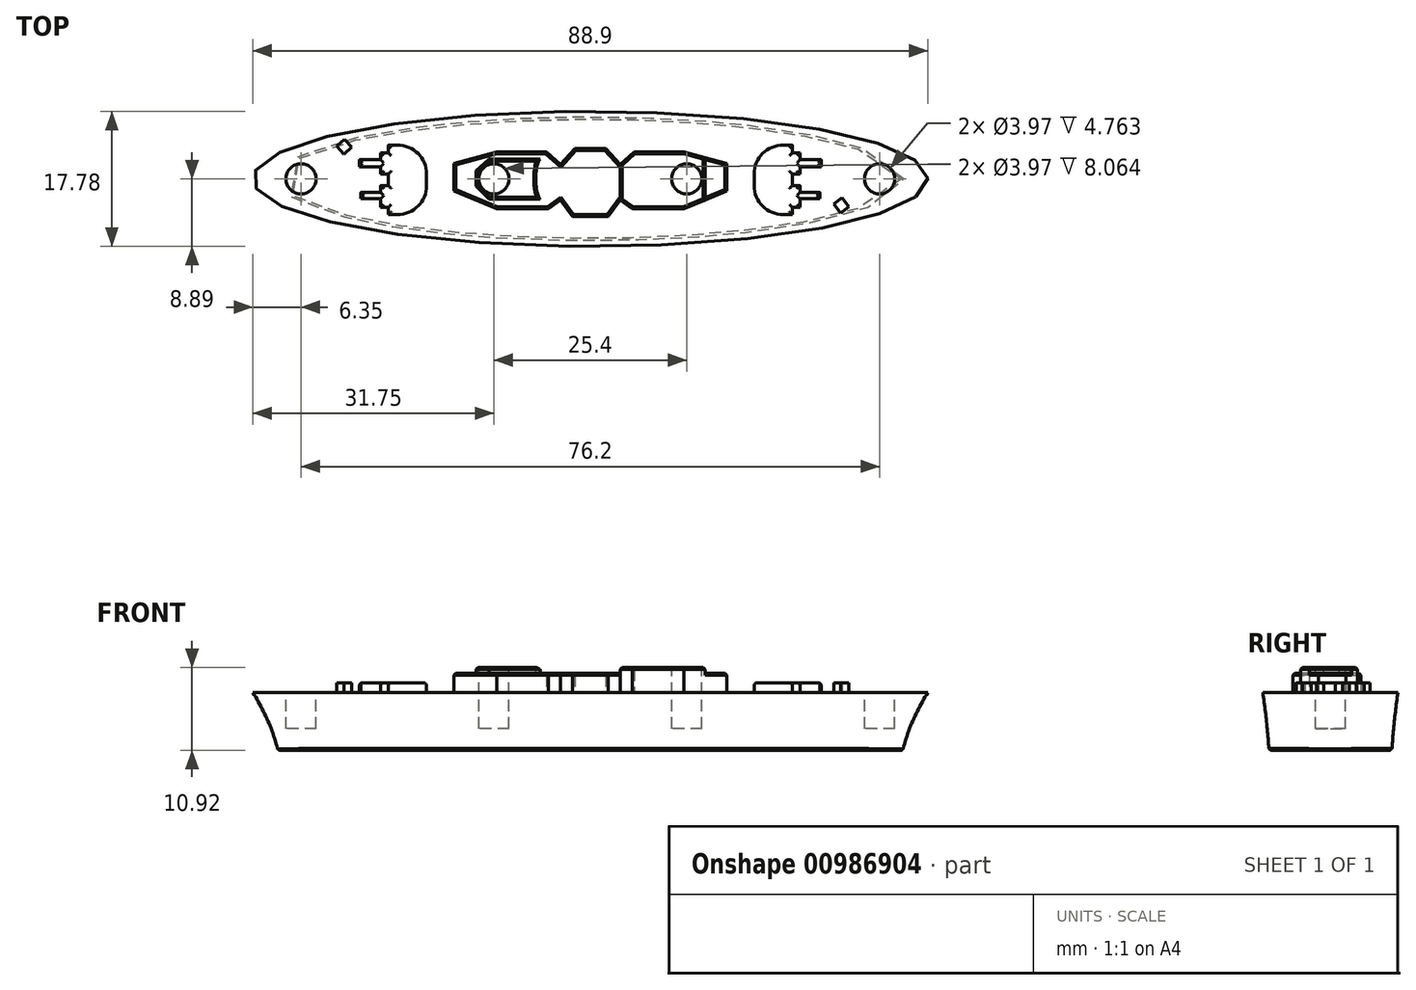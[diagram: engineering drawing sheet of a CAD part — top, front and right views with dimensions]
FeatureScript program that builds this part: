
annotation { "Feature Type Name" : "Feature", "Feature Type Description" : "" }
export const myFeature = defineFeature(function(context is Context, id is Id, definition is map)
    precondition{}
    {
        {
            var Q0;
            Q0=qCreatedBy(makeId("Top.planeOp"),FACE);
            var sketch = newSketch(context, id + "F0", { "sketchPlane" : qUnion([Q0])});
            skEllipse(sketch, "E0", {"center": v(0, 0) * mm, "majorRadius": 44.45 * mm, "minorRadius": 8.9 * mm, "majorAxis": v(1, 0)});
            skSolve(sketch);
        }
        {
            var Q0;
            Q0=qCreatedBy(makeId("Top.planeOp"),FACE);
            cPlane(context, id + "F1", {"entities" : qUnion([Q0]), "cplaneType" : CPlaneType.OFFSET, "offset" : 7.62 * mm, "oppositeDirection" : true, "width" : 152.4 * mm, "height" : 152.4 * mm});
        }
        {
            var Q0;
            Q0=qCreatedBy(id+"F1.planeOp",FACE);
            var sketch = newSketch(context, id + "F2", { "sketchPlane" : qUnion([Q0])});
            skEllipse(sketch, "E1", {"center": v(0, 0) * mm, "majorRadius": 41.16 * mm, "minorRadius": 8.1 * mm, "majorAxis": v(1, 0)});
            skSolve(sketch);
        }
        {
            var Q0;
            Q0=makeQuery(id+"F2.imprint","IMPRINT",FACE,{"disambiguationData":[TD([[makeQuery(id+"F2.imprint","IMPRINT",EDGE,{"derivedFrom":sQuery(id+"F2.wireOp",EDGE,"E1")}),1.0]])]});
            var Q1;
            Q1=makeQuery(id+"F0.imprint","IMPRINT",FACE,{"disambiguationData":[TD([[makeQuery(id+"F0.imprint","IMPRINT",EDGE,{"derivedFrom":sQuery(id+"F0.wireOp",EDGE,"E0")}),1.0]])]});
            loft(context, id + "F3", {"sheetProfilesArray" : [{ "sheetProfileEntities" : qUnion([Q0]) }, { "sheetProfileEntities" : qUnion([Q1]) }]});
        }
        {
            var Q0;
            Q0=makeQuery(id+"F3.opLoft","CAP_FACE",FACE,{"disambiguationData":[OSD([makeQuery(id+"F0.imprint","IMPRINT",FACE,{"disambiguationData":[TD([[makeQuery(id+"F0.imprint","IMPRINT",EDGE,{"derivedFrom":sQuery(id+"F0.wireOp",EDGE,"E0")}),1.0]])]})])],"isStart":true});
            var sketch = newSketch(context, id + "F4", { "sketchPlane" : qUnion([Q0])});
            skLineSegment(sketch, "E2", {"start": v(-38.1, 0) * mm, "end": v(-12.7, 0) * mm, "construction": true});
            skLineSegment(sketch, "E3", {"start": v(-12.7, 0) * mm, "end": v(12.7, 0) * mm, "construction": true});
            skLineSegment(sketch, "E4", {"start": v(12.7, 0) * mm, "end": v(38.1, 0) * mm, "construction": true});
            skCircle(sketch, "E5", {"center": v(38.1, 0) * mm, "radius": 1.98 * mm});
            skCircle(sketch, "E6", {"center": v(12.7, 0) * mm, "radius": 1.98 * mm});
            skCircle(sketch, "E7", {"center": v(-12.7, 0) * mm, "radius": 1.98 * mm});
            skCircle(sketch, "E8", {"center": v(-38.1, 0) * mm, "radius": 1.98 * mm});
            skSolve(sketch);
        }
        {
            var Q0;
            Q0=makeQuery(id+"F4.imprint","IMPRINT",FACE,{"disambiguationData":[TD([[makeQuery(id+"F4.imprint","IMPRINT",EDGE,{"derivedFrom":sQuery(id+"F4.wireOp",EDGE,"E8")}),1.0]])]});
            var Q1;
            Q1=makeQuery(id+"F4.imprint","IMPRINT",FACE,{"disambiguationData":[TD([[makeQuery(id+"F4.imprint","IMPRINT",EDGE,{"derivedFrom":sQuery(id+"F4.wireOp",EDGE,"E7")}),1.0]])]});
            var Q2;
            Q2=makeQuery(id+"F4.imprint","IMPRINT",FACE,{"disambiguationData":[TD([[makeQuery(id+"F4.imprint","IMPRINT",EDGE,{"derivedFrom":sQuery(id+"F4.wireOp",EDGE,"E6")}),1.0]])]});
            var Q3;
            Q3=makeQuery(id+"F4.imprint","IMPRINT",FACE,{"disambiguationData":[TD([[makeQuery(id+"F4.imprint","IMPRINT",EDGE,{"derivedFrom":sQuery(id+"F4.wireOp",EDGE,"E5")}),1.0]])]});
            extrude(context, id + "F5", {"entities" : qUnion([Q0, Q1, Q2, Q3]), "operationType" : NewBodyOperationType.REMOVE, "oppositeDirection" : true, "depth" : 4.76 * mm, "offsetDistance" : 25.4 * mm});
        }
        {
            var Q0;
            Q0=makeQuery(id+"F3.opLoft","CAP_FACE",FACE,{"disambiguationData":[OSD([makeQuery(id+"F0.imprint","IMPRINT",FACE,{"disambiguationData":[TD([[makeQuery(id+"F0.imprint","IMPRINT",EDGE,{"derivedFrom":sQuery(id+"F0.wireOp",EDGE,"E0")}),1.0]])]})])],"isStart":true});
            var sketch = newSketch(context, id + "F6", { "sketchPlane" : qUnion([Q0])});
            skLineSegment(sketch, "E9", {"start": v(0, 11.72) * mm, "end": v(0, 15.23) * mm, "construction": true});
            skLineSegment(sketch, "E10", {"start": v(0, 4) * mm, "end": v(2.05, 4) * mm});
            skLineSegment(sketch, "E11", {"start": v(2.05, 4) * mm, "end": v(3.92, 1.9) * mm});
            skLineSegment(sketch, "E12", {"start": v(3.92, 1.9) * mm, "end": v(5.78, 3.55) * mm});
            skLineSegment(sketch, "E13", {"start": v(5.78, 3.55) * mm, "end": v(12.33, 3.55) * mm});
            skLineSegment(sketch, "E14", {"start": v(12.33, 3.55) * mm, "end": v(17.96, 2.05) * mm});
            skLineSegment(sketch, "E15", {"start": v(17.96, 2.05) * mm, "end": v(17.96, -1.6) * mm});
            skLineSegment(sketch, "E16", {"start": v(17.96, -1.6) * mm, "end": v(12.33, -3.94) * mm});
            skLineSegment(sketch, "E17", {"start": v(12.33, -3.94) * mm, "end": v(5.55, -3.94) * mm});
            skLineSegment(sketch, "E18", {"start": v(5.55, -3.94) * mm, "end": v(3.92, -2.77) * mm});
            skLineSegment(sketch, "E19", {"start": v(3.92, -2.77) * mm, "end": v(2.37, -4.94) * mm});
            skLineSegment(sketch, "E20", {"start": v(2.37, -4.94) * mm, "end": v(0, -4.94) * mm});
            skLineSegment(sketch, "E21.MirrorCS", {"start": v(-5.55, -3.94) * mm, "end": v(-3.92, -2.77) * mm});
            skLineSegment(sketch, "E22.MirrorCS", {"start": v(-3.92, -2.77) * mm, "end": v(-2.37, -4.94) * mm});
            skLineSegment(sketch, "E23.MirrorCS", {"start": v(-2.05, 4) * mm, "end": v(-3.92, 1.9) * mm});
            skLineSegment(sketch, "E24.MirrorCS", {"start": v(-3.92, 1.9) * mm, "end": v(-5.78, 3.55) * mm});
            skLineSegment(sketch, "E25.MirrorCS", {"start": v(-2.37, -4.94) * mm, "end": v(0, -4.94) * mm});
            skLineSegment(sketch, "E26.MirrorCS", {"start": v(0, 4) * mm, "end": v(-2.05, 4) * mm});
            skLineSegment(sketch, "E27.MirrorCS", {"start": v(-17.96, -1.6) * mm, "end": v(-12.33, -3.94) * mm});
            skLineSegment(sketch, "E28.MirrorCS", {"start": v(-12.33, -3.94) * mm, "end": v(-5.55, -3.94) * mm});
            skLineSegment(sketch, "E29.MirrorCS", {"start": v(-17.96, 2.05) * mm, "end": v(-17.96, -1.6) * mm});
            skLineSegment(sketch, "E30.MirrorCS", {"start": v(-12.33, 3.55) * mm, "end": v(-17.96, 2.05) * mm});
            skLineSegment(sketch, "E31.MirrorCS", {"start": v(-5.78, 3.55) * mm, "end": v(-12.33, 3.55) * mm});
            skSolve(sketch);
        }
        {
            var Q0;
            Q0=makeQuery(id+"F6.imprint","IMPRINT",FACE,{"disambiguationData":[TD([[makeQuery(id+"F6.imprint","IMPRINT",EDGE,{"derivedFrom":sQuery(id+"F6.wireOp",EDGE,"E10")}),-1.0]])]});
            extrude(context, id + "F7", {"entities" : qUnion([Q0]), "operationType" : NewBodyOperationType.ADD, "depth" : 2.54 * mm, "offsetDistance" : 25.4 * mm});
        }
        {
            var Q0;
            Q0=makeQuery(id+"F7.opExtrude","CAP_FACE",FACE,{"disambiguationData":[OSD([sQuery(id+"F4.wireOp",EDGE,"E6"),sQuery(id+"F4.wireOp",EDGE,"E7"),sQuery(id+"F6.wireOp",EDGE,"E10"),sQuery(id+"F6.wireOp",EDGE,"E11"),sQuery(id+"F6.wireOp",EDGE,"E12"),sQuery(id+"F6.wireOp",EDGE,"E13"),sQuery(id+"F6.wireOp",EDGE,"E14"),sQuery(id+"F6.wireOp",EDGE,"E15"),sQuery(id+"F6.wireOp",EDGE,"E16"),sQuery(id+"F6.wireOp",EDGE,"E17"),sQuery(id+"F6.wireOp",EDGE,"E18"),sQuery(id+"F6.wireOp",EDGE,"E19"),sQuery(id+"F6.wireOp",EDGE,"E20"),sQuery(id+"F6.wireOp",EDGE,"E21.MirrorCS"),sQuery(id+"F6.wireOp",EDGE,"E22.MirrorCS"),sQuery(id+"F6.wireOp",EDGE,"E23.MirrorCS"),sQuery(id+"F6.wireOp",EDGE,"E24.MirrorCS"),sQuery(id+"F6.wireOp",EDGE,"E25.MirrorCS"),sQuery(id+"F6.wireOp",EDGE,"E26.MirrorCS"),sQuery(id+"F6.wireOp",EDGE,"E27.MirrorCS"),sQuery(id+"F6.wireOp",EDGE,"E28.MirrorCS"),sQuery(id+"F6.wireOp",EDGE,"E29.MirrorCS"),sQuery(id+"F6.wireOp",EDGE,"E30.MirrorCS"),sQuery(id+"F6.wireOp",EDGE,"E31.MirrorCS")])],"isStart":false});
            var sketch = newSketch(context, id + "F8", { "sketchPlane" : qUnion([Q0])});
            skLineSegment(sketch, "E32", {"start": v(-6.6, 2.58) * mm, "end": v(-13.36, 2.58) * mm});
            skLineSegment(sketch, "E33", {"start": v(-13.36, 2.58) * mm, "end": v(-15.07, 1.08) * mm});
            skLineSegment(sketch, "E34", {"start": v(-15.07, 1.08) * mm, "end": v(-15.07, -0.96) * mm});
            skLineSegment(sketch, "E35", {"start": v(-15.07, -0.96) * mm, "end": v(-13.36, -2.68) * mm});
            skLineSegment(sketch, "E36", {"start": v(-13.36, -2.68) * mm, "end": v(-6.6, -2.68) * mm});
            skPoint(sketch, "E37", {"position": v(-3.92, 1.08) * mm});
            skPoint(sketch, "E38", {"position": v(0, 3) * mm});
            skPoint(sketch, "E39", {"position": v(2.5, -0.42) * mm});
            skPoint(sketch, "E40", {"position": v(0, -3.64) * mm});
            skPoint(sketch, "E41", {"position": v(-3.92, -1.71) * mm});
            skFitSpline(sketch, "E42", {"points": [v(-6.6, 2.58) * mm, v(-3.92, 1.08) * mm, v(0, 3) * mm, v(2.5, -0.42) * mm, v(0, -3.64) * mm, v(-3.92, -1.71) * mm, v(-6.6, -2.68) * mm, v(-6.6, 2.58) * mm]});
            skLineSegment(sketch, "E43", {"start": v(5.78, 3.55) * mm, "end": v(3.92, 1.9) * mm});
            skLineSegment(sketch, "E44", {"start": v(3.92, 1.9) * mm, "end": v(3.92, -2.77) * mm});
            skLineSegment(sketch, "E45", {"start": v(3.92, -2.77) * mm, "end": v(5.55, -3.94) * mm});
            skLineSegment(sketch, "E46", {"start": v(5.55, -3.94) * mm, "end": v(12.33, -3.94) * mm});
            skLineSegment(sketch, "E47", {"start": v(12.33, -3.94) * mm, "end": v(15.14, -2.77) * mm});
            skLineSegment(sketch, "E48", {"start": v(15.14, -2.77) * mm, "end": v(15.14, 2.8) * mm});
            skLineSegment(sketch, "E49", {"start": v(15.14, 2.8) * mm, "end": v(12.33, 3.55) * mm});
            skLineSegment(sketch, "E50", {"start": v(12.33, 3.55) * mm, "end": v(5.78, 3.55) * mm});
            skSolve(sketch);
        }
        {
            var Q0;
            Q0=makeQuery(id+"F8.imprint","IMPRINT",FACE,{"disambiguationData":[TD([[makeQuery(id+"F8.imprint","IMPRINT",EDGE,{"derivedFrom":sQuery(id+"F8.wireOp",EDGE,"E32")}),1.0]])]});
            var Q1;
            Q1=makeQuery(id+"F8.imprint","IMPRINT",FACE,{"disambiguationData":[TD([[makeQuery(id+"F8.imprint","IMPRINT",EDGE,{"derivedFrom":sQuery(id+"F8.wireOp",EDGE,"E43")}),-1.0]])]});
            extrude(context, id + "F9", {"entities" : qUnion([Q0, Q1]), "operationType" : NewBodyOperationType.ADD, "depth" : 0.76 * mm, "offsetDistance" : 25.4 * mm});
        }
        {
            var Q0;
            Q0=makeQuery(id+"F3.opLoft","CAP_FACE",FACE,{"disambiguationData":[OSD([makeQuery(id+"F0.imprint","IMPRINT",FACE,{"disambiguationData":[TD([[makeQuery(id+"F0.imprint","IMPRINT",EDGE,{"derivedFrom":sQuery(id+"F0.wireOp",EDGE,"E0")}),1.0]])]})])],"isStart":true});
            var sketch = newSketch(context, id + "F10", { "sketchPlane" : qUnion([Q0])});
            skLineSegment(sketch, "E51", {"start": v(0, -10.91) * mm, "end": v(0, -13.7) * mm, "construction": true});
            skLineSegment(sketch, "E52.bottom", {"start": v(25.38, 4.45) * mm, "end": v(26.6, 4.45) * mm});
            skLineSegment(sketch, "E52.top", {"start": v(25.38, -4.7) * mm, "end": v(26.6, -4.7) * mm});
            skLineSegment(sketch, "E52.left", {"start": v(21.57, 0.64) * mm, "end": v(21.57, -0.9) * mm});
            skLineSegment(sketch, "E52.right", {"start": v(26.6, 4.45) * mm, "end": v(26.6, 3.41) * mm});
            skPoint(sketch, "E53.visualSharp", {"position": v(21.57, 4.45) * mm});
            skArc(sketch, "E53.filletArc", {"start": v(25.38, 4.45) * mm, "mid": v(22.68, 3.33) * mm, "end": v(21.57, 0.64) * mm});
            skPoint(sketch, "E54.visualSharp", {"position": v(21.57, -4.7) * mm});
            skArc(sketch, "E54.filletArc", {"start": v(21.57, -0.9) * mm, "mid": v(22.68, -3.6) * mm, "end": v(25.38, -4.7) * mm});
            skLineSegment(sketch, "E55.bottom", {"start": v(26.6, 3.41) * mm, "end": v(27.6, 3.41) * mm});
            skLineSegment(sketch, "E55.top", {"start": v(26.6, 0.62) * mm, "end": v(27.6, 0.62) * mm});
            skLineSegment(sketch, "E55.right", {"start": v(27.6, 3.41) * mm, "end": v(27.6, 2.5) * mm});
            skLineSegment(sketch, "E56.bottom", {"start": v(26.6, -0.89) * mm, "end": v(27.6, -0.89) * mm});
            skLineSegment(sketch, "E56.top", {"start": v(26.6, -3.75) * mm, "end": v(27.6, -3.75) * mm});
            skLineSegment(sketch, "E56.right", {"start": v(27.6, -0.89) * mm, "end": v(27.6, -1.8) * mm});
            skLineSegment(sketch, "E57.bottom", {"start": v(27.6, 2.5) * mm, "end": v(30.4, 2.5) * mm});
            skLineSegment(sketch, "E57.top", {"start": v(27.6, 1.6) * mm, "end": v(30.4, 1.6) * mm});
            skLineSegment(sketch, "E57.right", {"start": v(30.4, 2.5) * mm, "end": v(30.4, 1.6) * mm});
            skLineSegment(sketch, "E58.bottom", {"start": v(27.6, -1.8) * mm, "end": v(30.25, -1.8) * mm});
            skLineSegment(sketch, "E58.top", {"start": v(27.6, -2.62) * mm, "end": v(30.25, -2.62) * mm});
            skLineSegment(sketch, "E58.right", {"start": v(30.25, -1.8) * mm, "end": v(30.25, -2.62) * mm});
            skLineSegment(sketch, "E59.trimOffspring", {"start": v(27.6, 1.6) * mm, "end": v(27.6, 0.62) * mm});
            skLineSegment(sketch, "E60.trimOffspring", {"start": v(27.6, -2.62) * mm, "end": v(27.6, -3.75) * mm});
            skLineSegment(sketch, "E61.trimOffspring", {"start": v(26.6, -3.75) * mm, "end": v(26.6, -4.7) * mm});
            skLineSegment(sketch, "E62.trimOffspring", {"start": v(26.6, 0.62) * mm, "end": v(26.6, -0.89) * mm});
            skLineSegment(sketch, "E63.MirrorCS", {"start": v(-27.6, -0.89) * mm, "end": v(-27.6, -1.8) * mm});
            skLineSegment(sketch, "E64.MirrorCS", {"start": v(-26.6, -0.89) * mm, "end": v(-27.6, -0.89) * mm});
            skLineSegment(sketch, "E65.MirrorCS", {"start": v(-26.6, 0.62) * mm, "end": v(-27.6, 0.62) * mm});
            skLineSegment(sketch, "E66.MirrorCS", {"start": v(-27.6, 1.6) * mm, "end": v(-27.6, 0.62) * mm});
            skLineSegment(sketch, "E67.MirrorCS", {"start": v(-26.6, 0.62) * mm, "end": v(-26.6, -0.89) * mm});
            skLineSegment(sketch, "E68.MirrorCS", {"start": v(-27.6, -2.62) * mm, "end": v(-27.6, -3.75) * mm});
            skLineSegment(sketch, "E69.MirrorCS", {"start": v(-30.25, -1.8) * mm, "end": v(-30.25, -2.62) * mm});
            skLineSegment(sketch, "E70.MirrorCS", {"start": v(-26.6, -3.75) * mm, "end": v(-26.6, -4.7) * mm});
            skLineSegment(sketch, "E71.MirrorCS", {"start": v(-26.6, 3.41) * mm, "end": v(-27.6, 3.41) * mm});
            skLineSegment(sketch, "E72.MirrorCS", {"start": v(-21.57, 0.64) * mm, "end": v(-21.57, -0.9) * mm});
            skLineSegment(sketch, "E73.MirrorCS", {"start": v(-25.38, 4.45) * mm, "end": v(-26.6, 4.45) * mm});
            skLineSegment(sketch, "E74.MirrorCS", {"start": v(-26.6, -3.75) * mm, "end": v(-27.6, -3.75) * mm});
            skLineSegment(sketch, "E75.MirrorCS", {"start": v(-27.6, 3.41) * mm, "end": v(-27.6, 2.5) * mm});
            skLineSegment(sketch, "E76.MirrorCS", {"start": v(-30.4, 2.5) * mm, "end": v(-30.4, 1.6) * mm});
            skLineSegment(sketch, "E77.MirrorCS", {"start": v(-27.6, -2.62) * mm, "end": v(-30.25, -2.62) * mm});
            skLineSegment(sketch, "E78.MirrorCS", {"start": v(-27.6, -1.8) * mm, "end": v(-30.25, -1.8) * mm});
            skLineSegment(sketch, "E79.MirrorCS", {"start": v(-25.38, -4.7) * mm, "end": v(-26.6, -4.7) * mm});
            skLineSegment(sketch, "E80.MirrorCS", {"start": v(-26.6, 4.45) * mm, "end": v(-26.6, 3.41) * mm});
            skPoint(sketch, "E81.MirrorP", {"position": v(-21.57, -4.7) * mm});
            skArc(sketch, "E82.MirrorCS", {"start": v(-25.38, 4.45) * mm, "mid": v(-22.68, 3.33) * mm, "end": v(-21.57, 0.64) * mm});
            skArc(sketch, "E83.MirrorCS", {"start": v(-21.57, -0.9) * mm, "mid": v(-22.68, -3.6) * mm, "end": v(-25.38, -4.7) * mm});
            skPoint(sketch, "E84.MirrorP", {"position": v(-21.57, 4.45) * mm});
            skLineSegment(sketch, "E85.MirrorCS", {"start": v(-27.6, 1.6) * mm, "end": v(-30.4, 1.6) * mm});
            skLineSegment(sketch, "E86.MirrorCS", {"start": v(-27.6, 2.5) * mm, "end": v(-30.4, 2.5) * mm});
            skLineSegment(sketch, "E87", {"start": v(-32.4, 5.21) * mm, "end": v(-33.39, 4.3) * mm});
            skLineSegment(sketch, "E88", {"start": v(-33.39, 4.3) * mm, "end": v(-32.43, 3.25) * mm});
            skLineSegment(sketch, "E89", {"start": v(-32.43, 3.25) * mm, "end": v(-31.43, 4.16) * mm});
            skLineSegment(sketch, "E90", {"start": v(-31.43, 4.16) * mm, "end": v(-32.4, 5.21) * mm});
            skLineSegment(sketch, "E91", {"start": v(33.12, -2.5) * mm, "end": v(32.06, -3.33) * mm});
            skLineSegment(sketch, "E92", {"start": v(32.06, -3.33) * mm, "end": v(32.99, -4.52) * mm});
            skLineSegment(sketch, "E93", {"start": v(32.99, -4.52) * mm, "end": v(34.05, -3.69) * mm});
            skLineSegment(sketch, "E94", {"start": v(34.05, -3.69) * mm, "end": v(33.12, -2.5) * mm});
            skSolve(sketch);
        }
        {
            var Q0;
            Q0=makeQuery(id+"F10.imprint","IMPRINT",FACE,{"disambiguationData":[TD([[makeQuery(id+"F10.imprint","IMPRINT",EDGE,{"derivedFrom":sQuery(id+"F10.wireOp",EDGE,"E63.MirrorCS")}),1.0]])]});
            var Q1;
            Q1=makeQuery(id+"F10.imprint","IMPRINT",FACE,{"disambiguationData":[TD([[makeQuery(id+"F10.imprint","IMPRINT",EDGE,{"derivedFrom":sQuery(id+"F10.wireOp",EDGE,"E52.bottom")}),-1.0]])]});
            var Q2;
            Q2=makeQuery(id+"F10.imprint","IMPRINT",FACE,{"disambiguationData":[TD([[makeQuery(id+"F10.imprint","IMPRINT",EDGE,{"derivedFrom":sQuery(id+"F10.wireOp",EDGE,"E87")}),1.0]])]});
            var Q3;
            Q3=makeQuery(id+"F10.imprint","IMPRINT",FACE,{"disambiguationData":[TD([[makeQuery(id+"F10.imprint","IMPRINT",EDGE,{"derivedFrom":sQuery(id+"F10.wireOp",EDGE,"E91")}),1.0]])]});
            extrude(context, id + "F11", {"entities" : qUnion([Q0, Q1, Q2, Q3]), "operationType" : NewBodyOperationType.ADD, "depth" : 1.27 * mm, "offsetDistance" : 25.4 * mm});
        }
        {
            var Q0;
            Q0=makeQuery(id+"F11.opExtrude","CAP_FACE",FACE,{"disambiguationData":[OSD([sQuery(id+"F10.wireOp",EDGE,"E63.MirrorCS"),sQuery(id+"F10.wireOp",EDGE,"E64.MirrorCS"),sQuery(id+"F10.wireOp",EDGE,"E65.MirrorCS"),sQuery(id+"F10.wireOp",EDGE,"E66.MirrorCS"),sQuery(id+"F10.wireOp",EDGE,"E67.MirrorCS"),sQuery(id+"F10.wireOp",EDGE,"E68.MirrorCS"),sQuery(id+"F10.wireOp",EDGE,"E69.MirrorCS"),sQuery(id+"F10.wireOp",EDGE,"E70.MirrorCS"),sQuery(id+"F10.wireOp",EDGE,"E71.MirrorCS"),sQuery(id+"F10.wireOp",EDGE,"E72.MirrorCS"),sQuery(id+"F10.wireOp",EDGE,"E73.MirrorCS"),sQuery(id+"F10.wireOp",EDGE,"E74.MirrorCS"),sQuery(id+"F10.wireOp",EDGE,"E75.MirrorCS"),sQuery(id+"F10.wireOp",EDGE,"E76.MirrorCS"),sQuery(id+"F10.wireOp",EDGE,"E77.MirrorCS"),sQuery(id+"F10.wireOp",EDGE,"E78.MirrorCS"),sQuery(id+"F10.wireOp",EDGE,"E79.MirrorCS"),sQuery(id+"F10.wireOp",EDGE,"E80.MirrorCS"),sQuery(id+"F10.wireOp",EDGE,"E82.MirrorCS"),sQuery(id+"F10.wireOp",EDGE,"E83.MirrorCS"),sQuery(id+"F10.wireOp",EDGE,"E85.MirrorCS"),sQuery(id+"F10.wireOp",EDGE,"E86.MirrorCS")])],"isStart":false});
            var Q1;
            Q1=makeQuery(id+"F11.opExtrude","CAP_FACE",FACE,{"disambiguationData":[OSD([sQuery(id+"F10.wireOp",EDGE,"E52.bottom"),sQuery(id+"F10.wireOp",EDGE,"E52.top"),sQuery(id+"F10.wireOp",EDGE,"E52.left"),sQuery(id+"F10.wireOp",EDGE,"E52.right"),sQuery(id+"F10.wireOp",EDGE,"E53.filletArc"),sQuery(id+"F10.wireOp",EDGE,"E54.filletArc"),sQuery(id+"F10.wireOp",EDGE,"E55.bottom"),sQuery(id+"F10.wireOp",EDGE,"E55.top"),sQuery(id+"F10.wireOp",EDGE,"E55.right"),sQuery(id+"F10.wireOp",EDGE,"E56.bottom"),sQuery(id+"F10.wireOp",EDGE,"E56.top"),sQuery(id+"F10.wireOp",EDGE,"E56.right"),sQuery(id+"F10.wireOp",EDGE,"E57.bottom"),sQuery(id+"F10.wireOp",EDGE,"E57.top"),sQuery(id+"F10.wireOp",EDGE,"E57.right"),sQuery(id+"F10.wireOp",EDGE,"E58.bottom"),sQuery(id+"F10.wireOp",EDGE,"E58.top"),sQuery(id+"F10.wireOp",EDGE,"E58.right"),sQuery(id+"F10.wireOp",EDGE,"E59.trimOffspring"),sQuery(id+"F10.wireOp",EDGE,"E60.trimOffspring"),sQuery(id+"F10.wireOp",EDGE,"E61.trimOffspring"),sQuery(id+"F10.wireOp",EDGE,"E62.trimOffspring")])],"isStart":false});
            fillet(context, id + "F12", {"entities" : qUnion([Q0, Q1]), "radius" : 0.38 * mm, "tangentPropagation" : true, "allowEdgeOverflow" : false});
        }
        {
            var Q0;
            Q0=makeQuery(id+"F7.opExtrude","CAP_EDGE",EDGE,{"disambiguationData":[OSD([sQuery(id+"F6.wireOp",EDGE,"E20"),sQuery(id+"F6.wireOp",EDGE,"E25.MirrorCS")])],"isStart":false});
            var Q1;
            Q1=makeQuery(id+"F7.opExtrude","CAP_EDGE",EDGE,{"disambiguationData":[OSD([sQuery(id+"F6.wireOp",EDGE,"E19")])],"isStart":false});
            var Q2;
            Q2=makeQuery(id+"F7.opExtrude","CAP_EDGE",EDGE,{"disambiguationData":[OSD([sQuery(id+"F6.wireOp",EDGE,"E22.MirrorCS")])],"isStart":false});
            var Q3;
            Q3=makeQuery(id+"F7.opExtrude","CAP_EDGE",EDGE,{"disambiguationData":[OSD([sQuery(id+"F6.wireOp",EDGE,"E21.MirrorCS")])],"isStart":false});
            var Q4;
            Q4=makeQuery(id+"F7.opExtrude","CAP_EDGE",EDGE,{"disambiguationData":[OSD([sQuery(id+"F6.wireOp",EDGE,"E28.MirrorCS")])],"isStart":false});
            var Q5;
            Q5=makeQuery(id+"F7.opExtrude","CAP_EDGE",EDGE,{"disambiguationData":[OSD([sQuery(id+"F6.wireOp",EDGE,"E27.MirrorCS")])],"isStart":false});
            var Q6;
            Q6=makeQuery(id+"F7.opExtrude","CAP_EDGE",EDGE,{"disambiguationData":[OSD([sQuery(id+"F6.wireOp",EDGE,"E29.MirrorCS")])],"isStart":false});
            var Q7;
            Q7=makeQuery(id+"F7.opExtrude","CAP_EDGE",EDGE,{"disambiguationData":[OSD([sQuery(id+"F6.wireOp",EDGE,"E30.MirrorCS")])],"isStart":false});
            var Q8;
            Q8=makeQuery(id+"F7.opExtrude","CAP_EDGE",EDGE,{"disambiguationData":[OSD([sQuery(id+"F6.wireOp",EDGE,"E31.MirrorCS")])],"isStart":false});
            var Q9;
            Q9=makeQuery(id+"F7.opExtrude","CAP_EDGE",EDGE,{"disambiguationData":[OSD([sQuery(id+"F6.wireOp",EDGE,"E24.MirrorCS")])],"isStart":false});
            var Q10;
            Q10=makeQuery(id+"F7.opExtrude","CAP_EDGE",EDGE,{"disambiguationData":[OSD([sQuery(id+"F6.wireOp",EDGE,"E23.MirrorCS")])],"isStart":false});
            var Q11;
            Q11=makeQuery(id+"F7.opExtrude","CAP_EDGE",EDGE,{"disambiguationData":[OSD([sQuery(id+"F6.wireOp",EDGE,"E10"),sQuery(id+"F6.wireOp",EDGE,"E26.MirrorCS")])],"isStart":false});
            var Q12;
            Q12=makeQuery(id+"F7.opExtrude","CAP_EDGE",EDGE,{"disambiguationData":[OSD([sQuery(id+"F6.wireOp",EDGE,"E11")])],"isStart":false});
            var Q13;
            Q13=makeQuery(id+"F7.opExtrude","CAP_EDGE",EDGE,{"disambiguationData":[OSD([sQuery(id+"F6.wireOp",EDGE,"E16")])],"isStart":false});
            var Q14;
            Q14=makeQuery(id+"F7.opExtrude","CAP_EDGE",EDGE,{"disambiguationData":[OSD([sQuery(id+"F6.wireOp",EDGE,"E15")])],"isStart":false});
            var Q15;
            Q15=makeQuery(id+"F7.opExtrude","CAP_EDGE",EDGE,{"disambiguationData":[OSD([sQuery(id+"F6.wireOp",EDGE,"E14")])],"isStart":false});
            var Q16;
            Q16=makeQuery(id+"F9.opExtrude","CAP_EDGE",EDGE,{"disambiguationData":[OSD([sQuery(id+"F8.wireOp",EDGE,"E44")])],"isStart":false});
            var Q17;
            Q17=makeQuery(id+"F9.opExtrude","CAP_EDGE",EDGE,{"disambiguationData":[OSD([sQuery(id+"F8.wireOp",EDGE,"E45")])],"isStart":false});
            var Q18;
            Q18=makeQuery(id+"F9.opExtrude","CAP_EDGE",EDGE,{"disambiguationData":[OSD([sQuery(id+"F8.wireOp",EDGE,"E46")])],"isStart":false});
            var Q19;
            Q19=makeQuery(id+"F9.opExtrude","CAP_EDGE",EDGE,{"disambiguationData":[OSD([sQuery(id+"F8.wireOp",EDGE,"E47")])],"isStart":false});
            var Q20;
            Q20=makeQuery(id+"F9.opExtrude","CAP_EDGE",EDGE,{"disambiguationData":[OSD([sQuery(id+"F8.wireOp",EDGE,"E48")])],"isStart":false});
            var Q21;
            Q21=makeQuery(id+"F9.opExtrude","CAP_EDGE",EDGE,{"disambiguationData":[OSD([sQuery(id+"F8.wireOp",EDGE,"E49")])],"isStart":false});
            var Q22;
            Q22=makeQuery(id+"F9.opExtrude","CAP_EDGE",EDGE,{"disambiguationData":[OSD([sQuery(id+"F8.wireOp",EDGE,"E50")])],"isStart":false});
            var Q23;
            Q23=makeQuery(id+"F9.opExtrude","CAP_EDGE",EDGE,{"disambiguationData":[OSD([sQuery(id+"F8.wireOp",EDGE,"E43")])],"isStart":false});
            var Q24;
            Q24=makeQuery(id+"F9.opExtrude","CAP_EDGE",EDGE,{"disambiguationData":[OSD([sQuery(id+"F8.wireOp",EDGE,"E32")])],"isStart":false});
            var Q25;
            Q25=makeQuery(id+"F9.opExtrude","CAP_EDGE",EDGE,{"disambiguationData":[OSD([sQuery(id+"F8.wireOp",EDGE,"E36")])],"isStart":false});
            var Q26;
            Q26=makeQuery(id+"F9.opExtrude","CAP_EDGE",EDGE,{"disambiguationData":[OSD([sQuery(id+"F8.wireOp",EDGE,"E42")])],"isStart":false});
            var Q27;
            Q27=makeQuery(id+"F9.opExtrude","CAP_EDGE",EDGE,{"disambiguationData":[OSD([sQuery(id+"F8.wireOp",EDGE,"E33")])],"isStart":false});
            var Q28;
            Q28=makeQuery(id+"F9.opExtrude","CAP_EDGE",EDGE,{"disambiguationData":[OSD([sQuery(id+"F8.wireOp",EDGE,"E34")])],"isStart":false});
            var Q29;
            Q29=makeQuery(id+"F9.opExtrude","CAP_EDGE",EDGE,{"disambiguationData":[OSD([sQuery(id+"F8.wireOp",EDGE,"E35")])],"isStart":false});
            chamfer(context, id + "F13", {"entities" : qUnion([Q0, Q1, Q2, Q3, Q4, Q5, Q6, Q7, Q8, Q9, Q10, Q11, Q12, Q13, Q14, Q15, Q16, Q17, Q18, Q19, Q20, Q21, Q22, Q23, Q24, Q25, Q26, Q27, Q28, Q29]), "width" : 0.25 * mm, "tangentPropagation" : true});
        }
        {
            var Q0;
            Q0=makeQuery(id+"F3.opLoft","MID_CAP_EDGE",EDGE,{"disambiguationData":[OSD([sQuery(id+"F2.wireOp",EDGE,"E1")])],"capPos":0.0});
            var Q1;
            Q1=makeQuery(id+"F7.opExtrude","CAP_EDGE",EDGE,{"disambiguationData":[OSD([sQuery(id+"F6.wireOp",EDGE,"E27.MirrorCS")])],"isStart":true});
            var Q2;
            Q2=makeQuery(id+"F7.opExtrude","CAP_EDGE",EDGE,{"disambiguationData":[OSD([sQuery(id+"F6.wireOp",EDGE,"E28.MirrorCS")])],"isStart":true});
            var Q3;
            Q3=makeQuery(id+"F7.opExtrude","CAP_EDGE",EDGE,{"disambiguationData":[OSD([sQuery(id+"F6.wireOp",EDGE,"E21.MirrorCS")])],"isStart":true});
            var Q4;
            Q4=makeQuery(id+"F7.opExtrude","CAP_EDGE",EDGE,{"disambiguationData":[OSD([sQuery(id+"F6.wireOp",EDGE,"E22.MirrorCS")])],"isStart":true});
            var Q5;
            Q5=makeQuery(id+"F7.opExtrude","CAP_EDGE",EDGE,{"disambiguationData":[OSD([sQuery(id+"F6.wireOp",EDGE,"E20"),sQuery(id+"F6.wireOp",EDGE,"E25.MirrorCS")])],"isStart":true});
            var Q6;
            Q6=makeQuery(id+"F7.opExtrude","CAP_EDGE",EDGE,{"disambiguationData":[OSD([sQuery(id+"F6.wireOp",EDGE,"E19")])],"isStart":true});
            var Q7;
            Q7=makeQuery(id+"F7.opExtrude","CAP_EDGE",EDGE,{"disambiguationData":[OSD([sQuery(id+"F6.wireOp",EDGE,"E18")])],"isStart":true});
            var Q8;
            Q8=makeQuery(id+"F7.opExtrude","CAP_EDGE",EDGE,{"disambiguationData":[OSD([sQuery(id+"F6.wireOp",EDGE,"E17")])],"isStart":true});
            var Q9;
            Q9=makeQuery(id+"F7.opExtrude","CAP_EDGE",EDGE,{"disambiguationData":[OSD([sQuery(id+"F6.wireOp",EDGE,"E16")])],"isStart":true});
            var Q10;
            Q10=makeQuery(id+"F7.opExtrude","CAP_EDGE",EDGE,{"disambiguationData":[OSD([sQuery(id+"F6.wireOp",EDGE,"E15")])],"isStart":true});
            var Q11;
            Q11=makeQuery(id+"F7.opExtrude","CAP_EDGE",EDGE,{"disambiguationData":[OSD([sQuery(id+"F6.wireOp",EDGE,"E14")])],"isStart":true});
            var Q12;
            Q12=makeQuery(id+"F7.opExtrude","CAP_EDGE",EDGE,{"disambiguationData":[OSD([sQuery(id+"F6.wireOp",EDGE,"E13")])],"isStart":true});
            var Q13;
            Q13=makeQuery(id+"F7.opExtrude","CAP_EDGE",EDGE,{"disambiguationData":[OSD([sQuery(id+"F6.wireOp",EDGE,"E12")])],"isStart":true});
            var Q14;
            Q14=makeQuery(id+"F7.opExtrude","CAP_EDGE",EDGE,{"disambiguationData":[OSD([sQuery(id+"F6.wireOp",EDGE,"E11")])],"isStart":true});
            var Q15;
            Q15=makeQuery(id+"F7.opExtrude","CAP_EDGE",EDGE,{"disambiguationData":[OSD([sQuery(id+"F6.wireOp",EDGE,"E10"),sQuery(id+"F6.wireOp",EDGE,"E26.MirrorCS")])],"isStart":true});
            var Q16;
            Q16=makeQuery(id+"F7.opExtrude","CAP_EDGE",EDGE,{"disambiguationData":[OSD([sQuery(id+"F6.wireOp",EDGE,"E23.MirrorCS")])],"isStart":true});
            var Q17;
            Q17=makeQuery(id+"F7.opExtrude","CAP_EDGE",EDGE,{"disambiguationData":[OSD([sQuery(id+"F6.wireOp",EDGE,"E24.MirrorCS")])],"isStart":true});
            var Q18;
            Q18=makeQuery(id+"F7.opExtrude","CAP_EDGE",EDGE,{"disambiguationData":[OSD([sQuery(id+"F6.wireOp",EDGE,"E31.MirrorCS")])],"isStart":true});
            var Q19;
            Q19=makeQuery(id+"F7.opExtrude","CAP_EDGE",EDGE,{"disambiguationData":[OSD([sQuery(id+"F6.wireOp",EDGE,"E30.MirrorCS")])],"isStart":true});
            var Q20;
            Q20=makeQuery(id+"F7.opExtrude","CAP_EDGE",EDGE,{"disambiguationData":[OSD([sQuery(id+"F6.wireOp",EDGE,"E29.MirrorCS")])],"isStart":true});
            chamfer(context, id + "F14", {"entities" : qUnion([Q0, Q1, Q2, Q3, Q4, Q5, Q6, Q7, Q8, Q9, Q10, Q11, Q12, Q13, Q14, Q15, Q16, Q17, Q18, Q19, Q20]), "width" : 0.25 * mm, "tangentPropagation" : true});
        }
    });
